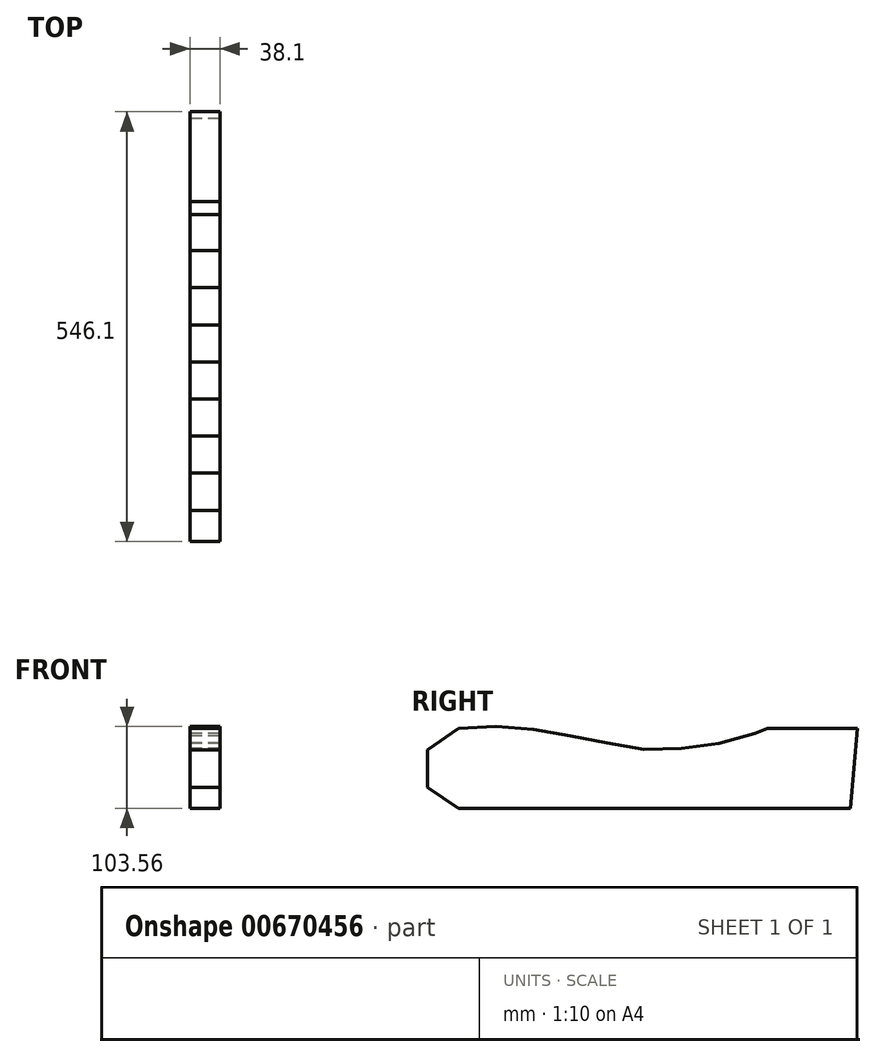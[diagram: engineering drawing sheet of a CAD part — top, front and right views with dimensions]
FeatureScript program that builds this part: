
annotation { "Feature Type Name" : "Feature", "Feature Type Description" : "" }
export const myFeature = defineFeature(function(context is Context, id is Id, definition is map)
    precondition{}
    {
        {
            var Q0;
            Q0=qCreatedBy(makeId("Right.planeOp"),FACE);
            var sketch = newSketch(context, id + "F0", { "sketchPlane" : qUnion([Q0])});
            skLineSegment(sketch, "E0", {"start": v(-76.48, 0) * mm, "end": v(421.35, 0) * mm});
            skLineSegment(sketch, "E1", {"start": v(-76.48, 0) * mm, "end": v(-115.91, 26.7) * mm});
            skLineSegment(sketch, "E2", {"start": v(-115.91, 26.7) * mm, "end": v(-115.91, 74.32) * mm});
            skLineSegment(sketch, "E3", {"start": v(-115.91, 74.32) * mm, "end": v(-76.48, 101.02) * mm});
            skLineSegment(sketch, "E4", {"start": v(-76.48, 101.02) * mm, "end": v(315.89, 101.02) * mm, "construction": true});
            skLineSegment(sketch, "E5", {"start": v(315.89, 101.02) * mm, "end": v(430.19, 101.02) * mm});
            skLineSegment(sketch, "E6", {"start": v(421.35, 0) * mm, "end": v(430.19, 101.02) * mm});
            skFitSpline(sketch, "E7", {"points": [v(-76.48, 101.02) * mm, v(163.49, 75.62) * mm, v(315.89, 101.02) * mm], "startDerivative": vector(500.26, 63.93) * mm, "endDerivative": vector(249.22, 107.9) * mm, "construction": true});
            skLineSegment(sketch, "E8", {"start": v(315.89, 101.02) * mm, "end": v(163.49, 101.02) * mm, "construction": true});
            skLineSegment(sketch, "E9", {"start": v(163.49, 101.02) * mm, "end": v(163.49, 75.62) * mm, "construction": true});
            skCircle(sketch, "E10", {"center": v(-71.04, 50.5) * mm, "radius": 50.8 * mm, "construction": true});
            skLineSegment(sketch, "E11", {"start": v(-28.92, 103.56) * mm, "end": v(18.56, 99.83) * mm});
            skLineSegment(sketch, "E12", {"start": v(18.56, 99.83) * mm, "end": v(65.51, 91.86) * mm});
            skLineSegment(sketch, "E13", {"start": v(65.51, 91.86) * mm, "end": v(112.24, 82.62) * mm});
            skLineSegment(sketch, "E14", {"start": v(112.24, 82.62) * mm, "end": v(159.23, 74.9) * mm});
            skLineSegment(sketch, "E15", {"start": v(159.23, 74.9) * mm, "end": v(206.85, 75.66) * mm});
            skLineSegment(sketch, "E16", {"start": v(206.85, 75.66) * mm, "end": v(254.04, 82.06) * mm});
            skLineSegment(sketch, "E17", {"start": v(254.04, 82.06) * mm, "end": v(299.95, 94.75) * mm});
            skLineSegment(sketch, "E18", {"start": v(-28.92, 103.56) * mm, "end": v(-76.48, 101.02) * mm});
            skLineSegment(sketch, "E19", {"start": v(299.95, 94.75) * mm, "end": v(315.89, 101.02) * mm});
            skSolve(sketch);
        }
        {
            var Q0;
            Q0=makeQuery(id+"F0.imprint","IMPRINT",FACE,{"disambiguationData":[TD([[makeQuery(id+"F0.imprint","IMPRINT",EDGE,{"derivedFrom":sQuery(id+"F0.wireOp",EDGE,"E0")}),1.0]])]});
            extrude(context, id + "F1", {"entities" : qUnion([Q0]), "depth" : 38.1 * mm, "offsetDistance" : 25.4 * mm});
        }
    });
